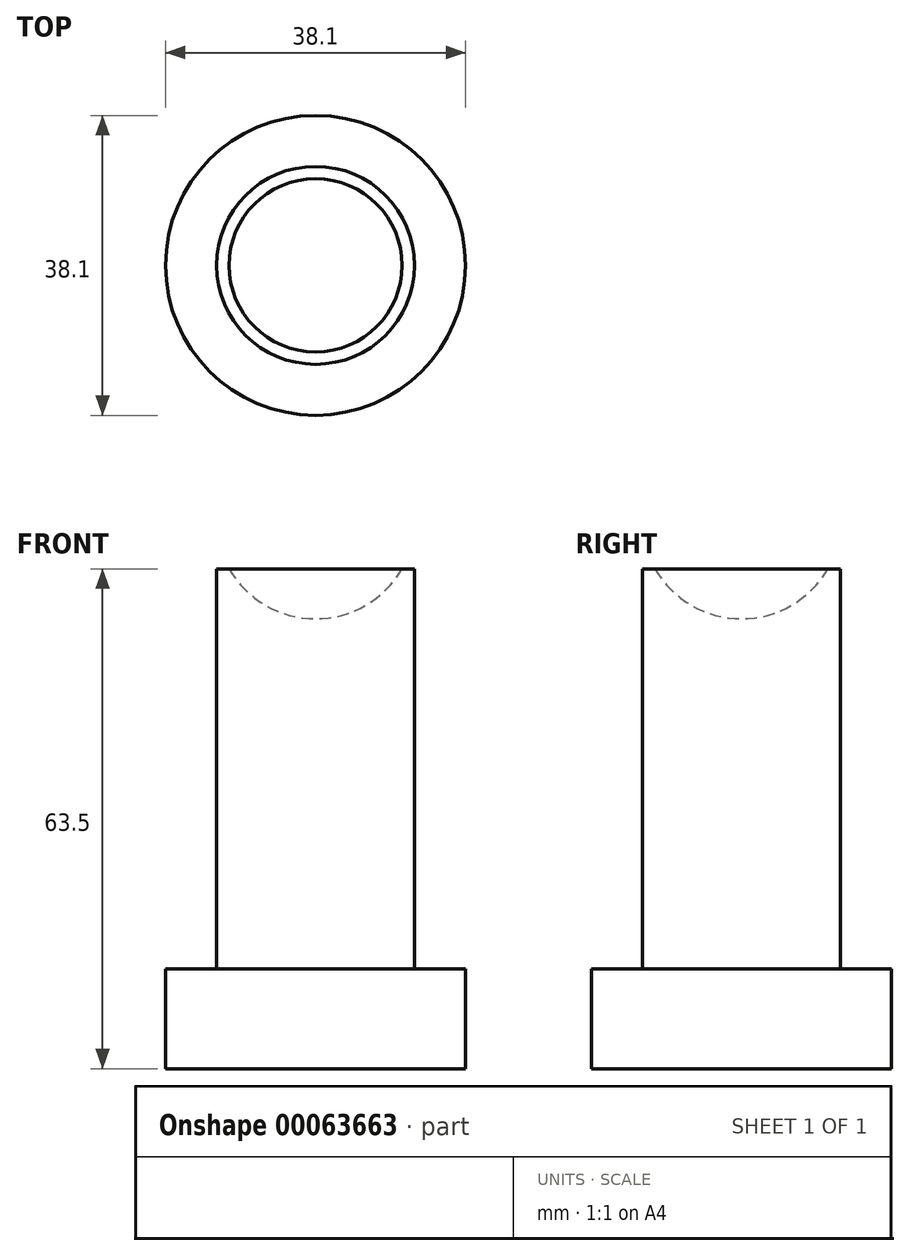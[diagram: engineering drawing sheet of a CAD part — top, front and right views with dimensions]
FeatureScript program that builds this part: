
annotation { "Feature Type Name" : "Feature", "Feature Type Description" : "" }
export const myFeature = defineFeature(function(context is Context, id is Id, definition is map)
    precondition{}
    {
        {
            var Q0;
            Q0=qCreatedBy(makeId("Top.planeOp"),FACE);
            var sketch = newSketch(context, id + "F0", { "sketchPlane" : qUnion([Q0])});
            skCircle(sketch, "E0", {"center": v(0, 0) * mm, "radius": 19.05 * mm});
            skSolve(sketch);
        }
        {
            var Q0;
            Q0=makeQuery(id+"F0.imprint","IMPRINT",FACE,{"disambiguationData":[TD([[makeQuery(id+"F0.imprint","IMPRINT",EDGE,{"derivedFrom":sQuery(id+"F0.wireOp",EDGE,"E0")}),1.0]])]});
            extrude(context, id + "F1", {"entities" : qUnion([Q0]), "depth" : 12.7 * mm});
        }
        {
            var Q0;
            Q0=makeQuery(id+"F1.opExtrude","CAP_FACE",FACE,{"disambiguationData":[OSD([sQuery(id+"F0.wireOp",EDGE,"E0")])],"isStart":false});
            var sketch = newSketch(context, id + "F2", { "sketchPlane" : qUnion([Q0])});
            skCircle(sketch, "E1", {"center": v(0, 0) * mm, "radius": 12.57 * mm});
            skSolve(sketch);
        }
        {
            var Q0;
            Q0=makeQuery(id+"F2.imprint","IMPRINT",FACE,{"disambiguationData":[TD([[makeQuery(id+"F2.imprint","IMPRINT",EDGE,{"derivedFrom":sQuery(id+"F2.wireOp",EDGE,"E1")}),1.0]])]});
            extrude(context, id + "F3", {"entities" : qUnion([Q0]), "depth" : 50.8 * mm});
        }
        {
            var Q0;
            Q0=qCreatedBy(makeId("Right.planeOp"),FACE);
            var sketch = newSketch(context, id + "F4", { "sketchPlane" : qUnion([Q0])});
            skArc(sketch, "E2", {"start": v(-12.7, 69.85) * mm, "mid": v(0, 57.15) * mm, "end": v(12.7, 69.85) * mm});
            skLineSegment(sketch, "E3", {"start": v(12.7, 69.85) * mm, "end": v(-12.7, 69.85) * mm});
            skSolve(sketch);
        }
        {
            var Q0;
            Q0=makeQuery(id+"F4.imprint","IMPRINT",FACE,{"disambiguationData":[TD([[makeQuery(id+"F4.imprint","IMPRINT",EDGE,{"derivedFrom":sQuery(id+"F4.wireOp",EDGE,"E2")}),1.0]])]});
            var Q1;
            Q1=sQuery(id+"F4.wireOp",EDGE,"E3");
            revolve(context, id + "F5", {"operationType" : NewBodyOperationType.REMOVE, "entities" : qUnion([Q0]), "axis" : qUnion([Q1]), "revolveType" : RevolveType.FULL, "oppositeDirection" : true});
        }
    });
